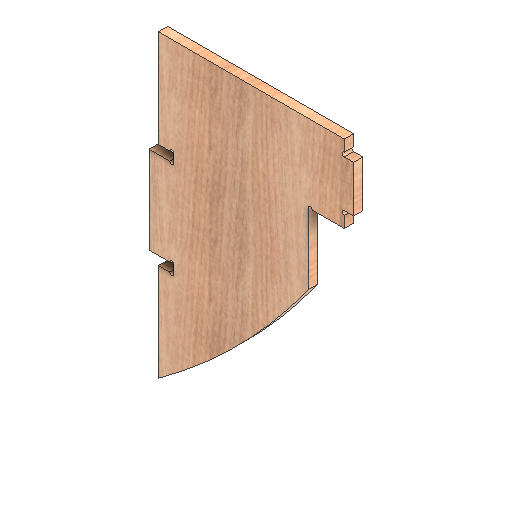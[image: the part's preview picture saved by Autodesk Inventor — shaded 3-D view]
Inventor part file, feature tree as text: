
AUTODESK INVENTOR PART (.ipt)
format: ipt  version: 2021 (Build 250183000, 183)  size: 226,304 bytes
history: native  units: mm
features: other x2, extrude x1
ambient origin geometry x8: Origin, YZ Plane, XZ Plane, XY Plane, X Axis, Y Axis, Z Axis, Center Point
bodies: Solid1 (feature_tree)
feature tree (3):
  other  "CONTOURS"
  other  "LETTERS"
  extrude  "Extrusion1"  Depth=18.0mm TaperAngle=0.0deg
